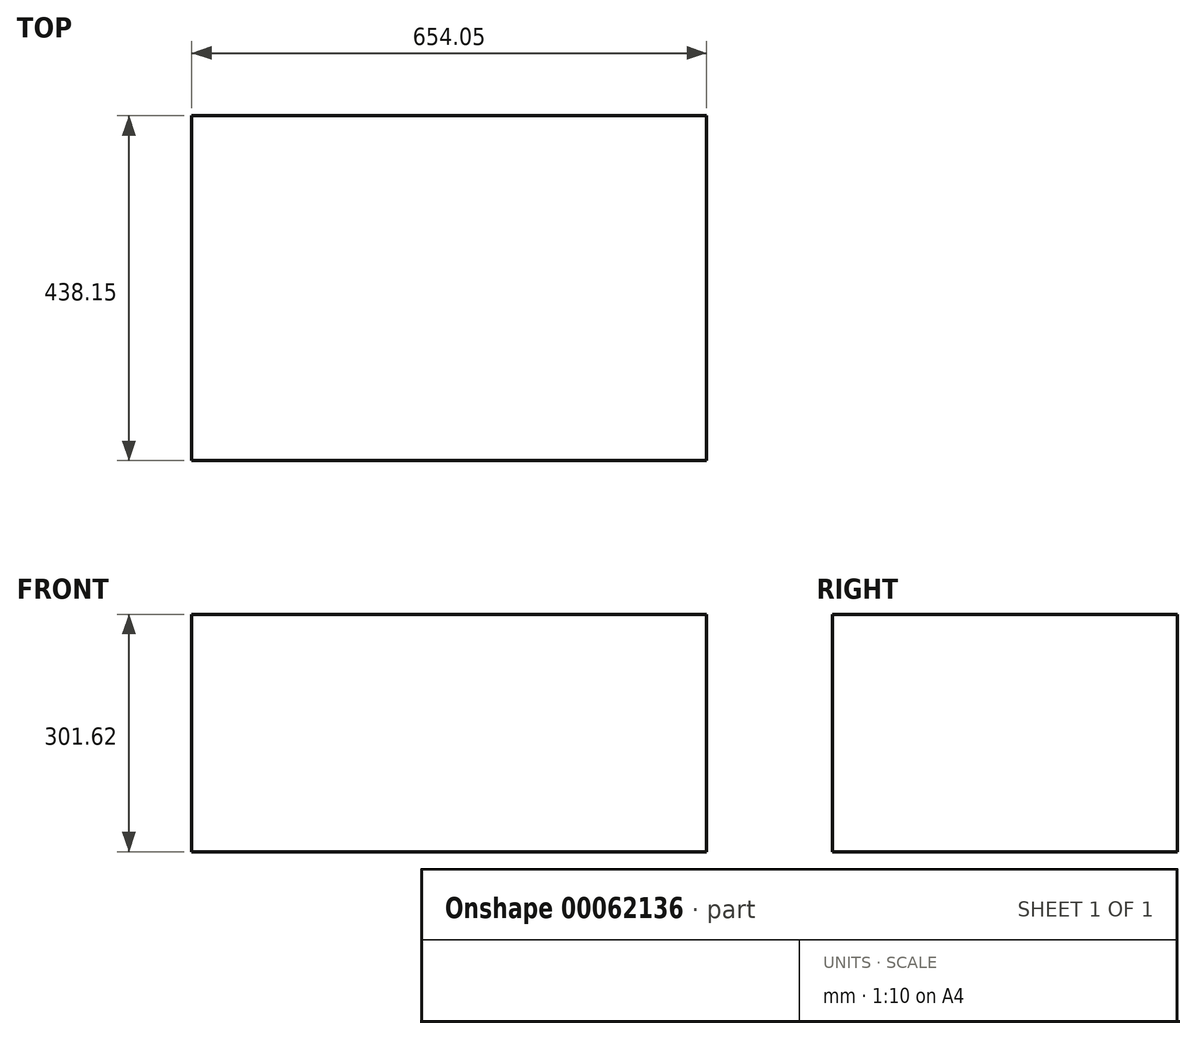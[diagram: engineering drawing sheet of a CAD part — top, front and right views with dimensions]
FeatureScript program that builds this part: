
annotation { "Feature Type Name" : "Feature", "Feature Type Description" : "" }
export const myFeature = defineFeature(function(context is Context, id is Id, definition is map)
    precondition{}
    {
        {
            var Q0;
            Q0=qCreatedBy(makeId("Top.planeOp"),FACE);
            var sketch = newSketch(context, id + "F0", { "sketchPlane" : qUnion([Q0])});
            skLineSegment(sketch, "E0.bottom", {"start": v(-306.86, 247.4) * mm, "end": v(347.19, 247.4) * mm});
            skLineSegment(sketch, "E0.top", {"start": v(-306.86, -190.74) * mm, "end": v(347.19, -190.74) * mm});
            skLineSegment(sketch, "E0.left", {"start": v(-306.86, 247.4) * mm, "end": v(-306.86, -190.74) * mm});
            skLineSegment(sketch, "E0.right", {"start": v(347.19, 247.4) * mm, "end": v(347.19, -190.74) * mm});
            skSolve(sketch);
        }
        {
            var Q0;
            Q0=makeQuery(id+"F0.imprint","IMPRINT",FACE,{"disambiguationData":[TD([[makeQuery(id+"F0.imprint","IMPRINT",EDGE,{"derivedFrom":sQuery(id+"F0.wireOp",EDGE,"E0.bottom")}),-1.0]])]});
            extrude(context, id + "F1", {"entities" : qUnion([Q0]), "depth" : 301.62 * mm});
        }
    });
